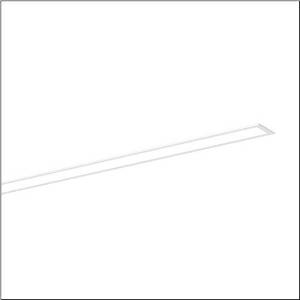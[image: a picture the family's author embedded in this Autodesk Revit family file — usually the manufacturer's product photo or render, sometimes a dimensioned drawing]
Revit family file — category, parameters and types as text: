
# Revit family: silica_21_51mx10tat2w
name_source: partatom
category: Lighting Fixtures
units: mm (PartAtom-declared; Revit-internal decimal feet)

## family parameters
Cut with Voids When Loaded = No
Host = Face
Light Source = No
Part Type = Normal
Room Calculation Point = No
Round Connector Dimension = Use Diameter
Shared = No

## types (1)
- --- (1 x LED, 2400 lm, 20.5 W, 6500K)
    Apparent Load = 21 VA
    CIE Flux Codes = 48 79 96 100 100
    Color Rendering = 80
    Color Temperature = 6500K
    Default Elevation = 1800 mm
    Description = Silica 21, office luminaire, primary optical cover: cover, of PMMA, opal, light emission: direct distribution, primary light characteristic: symmetric, installation type: recessed, LED, rated luminous flux: 2.400lm, luminous efficacy: 112lm/W, light colour: 8tw, colour temperature: 2700..6500K, control gear: DALI DT8, with terminal, 3+2-pole, max. 2.5mm², mains connection: 220..240V, AC, 50/60Hz, rated input power: 21.5W, luminaire housing, of aluminium, traffic white (RAL 9016), length: 1.228mm, width: 79mm, height: 53mm, protection rating (complete): IP20, insulation class (complete): insulation class I (protective earthing), certification: CE, ENEC, VDE, permissible operating ambient temperature: 0..+35°C, standard: EN 50419, packaging unit: 1 piece
    Height = 0 mm  [stored 0 ft]
    Lamp = 1 x LED
    Lamp Light Flux = 2400 lm
    Lamp Power = 20.5 W
    Lamp count = 1
    Length = 1227 mm
    Luminous efficacy = 117 lm/W
    Manufacturer = Siteco
    ModVariant = No
    Model = 51MX10TAT2W
    Mounting Place = Ceiling
    Mounting Type = Recessed
    Number of Poles = 1
    OnlyDefault = Yes
    Power Factor = 1
    Product Name = Silica 21
    Product group = office luminaire | ceiling recessed
    ProductGroupID = 400
    Protection Class = Protection class I
    Protection Degree = IP 20
    RLX_Detail_Level = 1
    RLX_Emergency_Light_Flux = 0 lm
    RLX_Emergency_Type = 0
    RLX_Emergency_Type_DB = No
    RlxData = <blob elided: 17997 chars, md5=139df32b>
    Socket = socket
    Standby Power = 0 W
    System Light Flux = 2400 lm
    System Power = 21 W
    Type Comments = individual setting
    Type Image = l_1335891.jpg
    URL = http://relux.com
    VarID = @adj_139223
    Voltage = 0 V
    Weight = 0.00 kg
    Width = 79 mm

note: [stored X ft] marks values corroborated as IEEE doubles in the binary element streams (Revit-internal decimal feet)

## geometry (parser evidence)
native form markers: Blend x4, Sweep x12
no freeform markers — native parametric forms only
